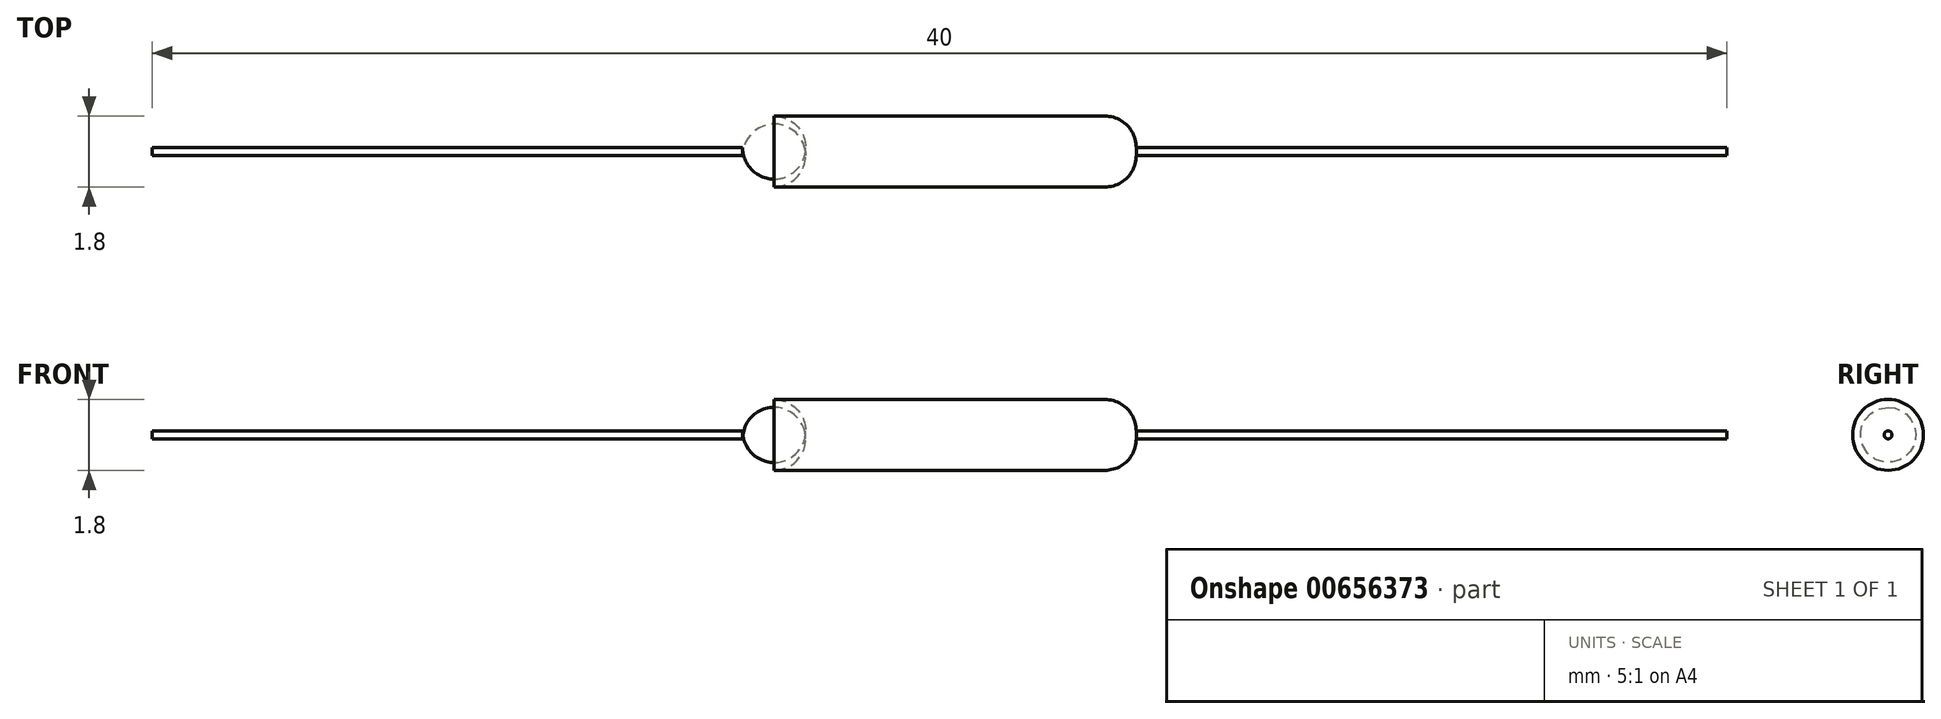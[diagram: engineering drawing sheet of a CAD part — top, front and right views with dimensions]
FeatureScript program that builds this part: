
annotation { "Feature Type Name" : "Feature", "Feature Type Description" : "" }
export const myFeature = defineFeature(function(context is Context, id is Id, definition is map)
    precondition{}
    {
        {
            var Q0;
            Q0=qCreatedBy(makeId("Top.planeOp"),FACE);
            var sketch = newSketch(context, id + "F0", { "sketchPlane" : qUnion([Q0])});
            skLineSegment(sketch, "E0", {"start": v(-10, 0) * mm, "end": v(0, 0) * mm});
            skSolve(sketch);
        }
        {
            var Q0;
            Q0=qCreatedBy(makeId("Right.planeOp"),FACE);
            var sketch = newSketch(context, id + "F1", { "sketchPlane" : qUnion([Q0])});
            skCircle(sketch, "E1", {"center": v(0, 0) * mm, "radius": 0.9 * mm});
            skSolve(sketch);
        }
        {
            var Q0;
            Q0=makeQuery(id+"F1.imprint","IMPRINT",FACE,{"disambiguationData":[TD([[makeQuery(id+"F1.imprint","IMPRINT",EDGE,{"derivedFrom":sQuery(id+"F1.wireOp",EDGE,"E1")}),1.0]])]});
            var Q1;
            Q1=sQuery(id+"F0.wireOp",EDGE,"E0");
            sweep(context, id + "F2", {"profiles" : qUnion([Q0]), "path" : qUnion([Q1])});
        }
        {
            var Q0;
            Q0=makeQuery(id+"F2.opSweep","CAP_EDGE",EDGE,{"disambiguationData":[OSD([sQuery(id+"F0.wireOp",VERTEX,"E0.end"),sQuery(id+"F1.wireOp",EDGE,"E1")])],"isStart":true});
            var Q1;
            Q1=makeQuery(id+"F2.opSweep","CAP_EDGE",EDGE,{"disambiguationData":[OSD([sQuery(id+"F0.wireOp",VERTEX,"E0.start"),sQuery(id+"F1.wireOp",EDGE,"E1")])],"isStart":false});
            fillet(context, id + "F3", {"entities" : qUnion([Q0, Q1]), "radius" : 0.8 * mm, "tangentPropagation" : true, "allowEdgeOverflow" : false});
        }
        {
            var Q0;
            Q0=qCreatedBy(makeId("Top.planeOp"),FACE);
            var sketch = newSketch(context, id + "F4", { "sketchPlane" : qUnion([Q0])});
            skLineSegment(sketch, "E2", {"start": v(0, 0) * mm, "end": v(15, 0) * mm});
            skSolve(sketch);
        }
        {
            var Q0;
            Q0=makeQuery(id+"F2.opSweep","CAP_FACE",FACE,{"disambiguationData":[OSD([sQuery(id+"F0.wireOp",VERTEX,"E0.end"),sQuery(id+"F1.wireOp",EDGE,"E1")])],"isStart":true});
            var Q1;
            Q1=sQuery(id+"F4.wireOp",EDGE,"E2");
            sweep(context, id + "F5", {"operationType" : NewBodyOperationType.ADD, "profiles" : qUnion([Q0]), "path" : qUnion([Q1])});
        }
        {
            var Q0;
            Q0=qCreatedBy(makeId("Top.planeOp"),FACE);
            var sketch = newSketch(context, id + "F6", { "sketchPlane" : qUnion([Q0])});
            skLineSegment(sketch, "E3", {"start": v(-10, 0) * mm, "end": v(-25, 0) * mm});
            skSolve(sketch);
        }
        {
            var Q0;
            Q0=makeQuery(id+"F2.opSweep","CAP_FACE",FACE,{"disambiguationData":[OSD([sQuery(id+"F0.wireOp",VERTEX,"E0.start"),sQuery(id+"F1.wireOp",EDGE,"E1")])],"isStart":false});
            var Q1;
            Q1=sQuery(id+"F6.wireOp",EDGE,"E3");
            sweep(context, id + "F7", {"operationType" : NewBodyOperationType.ADD, "profiles" : qUnion([Q0]), "path" : qUnion([Q1])});
        }
    });
